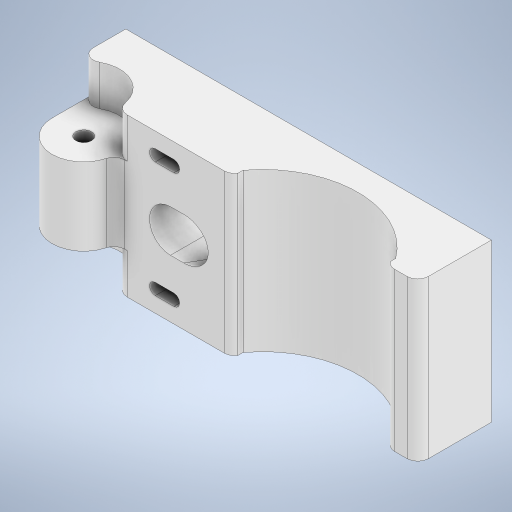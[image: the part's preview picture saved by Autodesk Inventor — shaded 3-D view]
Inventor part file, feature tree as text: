
AUTODESK INVENTOR PART (.ipt)
format: ipt  version: 2023 (Build 270158000, 158)  size: 371,712 bytes
history: native  units: mm
features: sketch x8, extrude x4, other x3, fillet x1, plane x1, loft x1, projected_geometry x1
ambient origin geometry x8: Origin, YZ Plane, XZ Plane, XY Plane, X Axis, Y Axis, Z Axis, Center Point
bodies: Solid1 (feature_tree)
feature tree (19):
  sketch  "Sketch2"  dims[d3=2.0mm d17=3.0mm]
  extrude  "Extrusion1"  Depth=3.0mm
  extrude  "Extrusion2"  Depth=30.0mm TaperAngle=0.0deg
  extrude  "Extrusion10"  Depth=1.0mm
  fillet  "Fillet4"  Radius=1.0mm
  sketch  "Sketch18"  dims[d18=2.0mm d26=30.0mm d27=0.0mm]
  plane  "Work Plane3"
  sketch  "Sketch19"  dims[d28=14.7mm d29=0.0mm d59=1.0mm d60=1.0mm]
  sketch  "3D Sketch1"
  sketch  "Sketch20"  dims[d62=10.0mm d63=0.0mm d95=2.0mm]
  sketch  "3D Sketch2"
  loft  "Loft1"
  extrude  "Extrusion21"  Depth=12.0mm
  other  "Project to Surface1"
  other  "Project to Surface2"
  other  "Project to Surface3"
  sketch  "Sketch21"  dims[d137=2.199496mm d140=12.0mm]
  projected_geometry  "Projected Loop1"
  sketch  "Sketch22"  dims[d141=69.5mm d142=14.0mm d143=6.0mm d144=17.5mm d145=19.0mm d146=5.4mm d147=6.225mm d148=13.4mm d149=16.5mm d151=30.0deg d152=90.0deg d153=8.0mm d154=16.5mm d155=8.0mm d156=10.635463mm d157=0.0mm d158=90.0deg d159=0.0mm d160=90.0deg d165=4.5mm d166=0.0mm d167=11.0mm d168=8.5mm d169=2.2mm d45=0.0mm d46=0.0mm d47=0.0mm d48=0.0mm d52=0.0mm d53=0.0mm d54=0.0mm d55=0.0mm d67=0.5mm d68=0.872665mm d69=0.5mm d70=0.872665mm d122=0.5mm d123=0.872665mm d124=0.5mm d125=0.872665mm]
